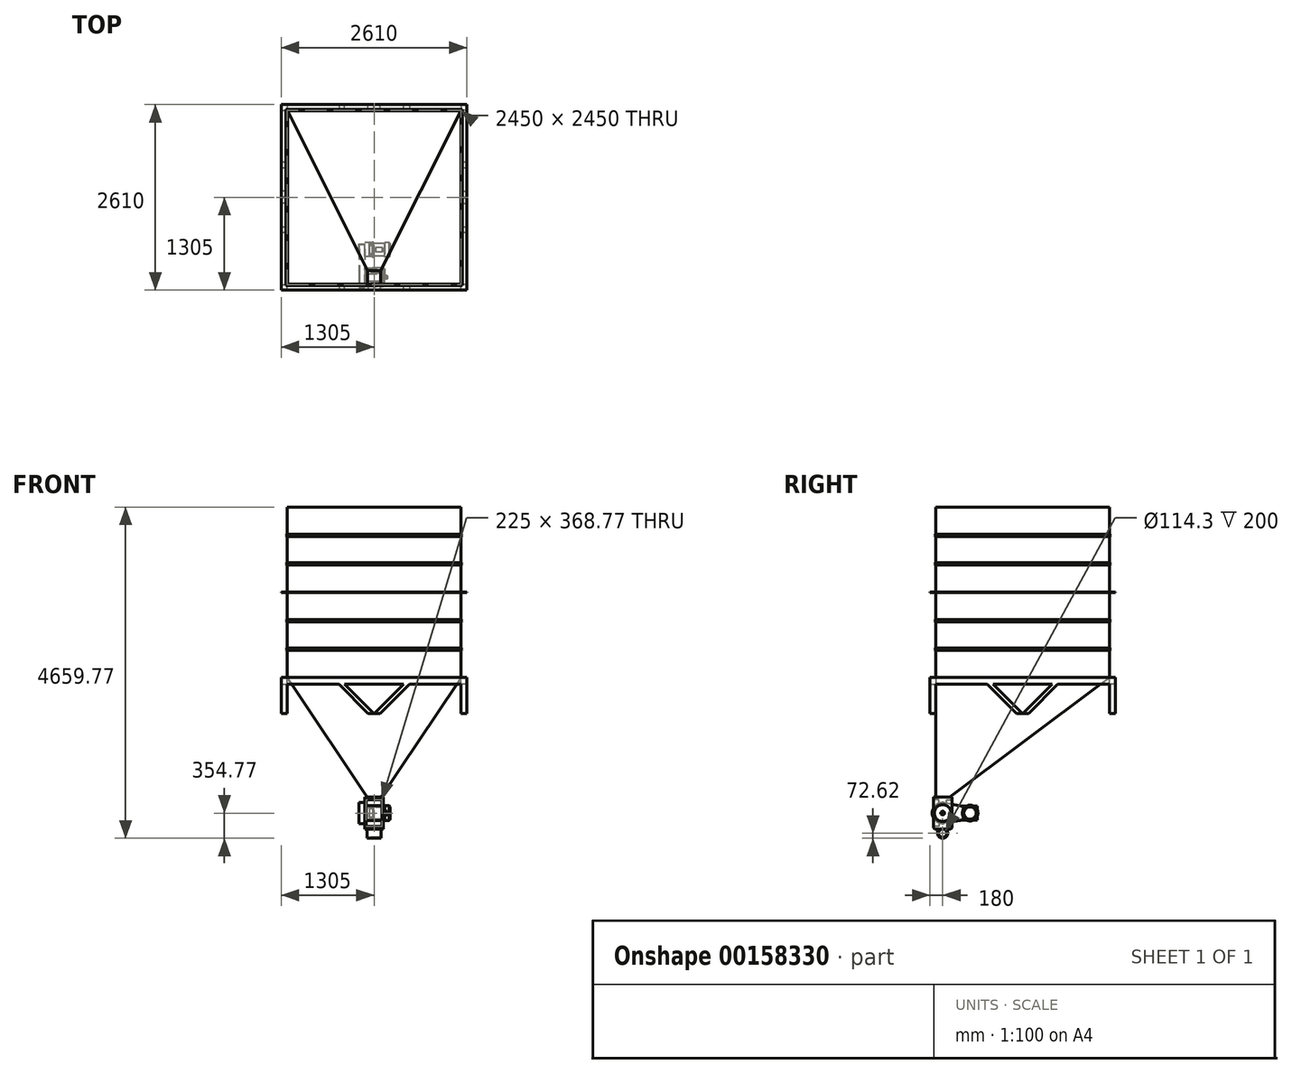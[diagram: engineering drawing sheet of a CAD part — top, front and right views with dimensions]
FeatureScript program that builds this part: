
annotation { "Feature Type Name" : "Feature", "Feature Type Description" : "" }
export const myFeature = defineFeature(function(context is Context, id is Id, definition is map)
    precondition{}
    {
        {
            var Q0;
            Q0=qCreatedBy(makeId("Top.planeOp"),FACE);
            var sketch = newSketch(context, id + "F0", { "sketchPlane" : qUnion([Q0])});
            skLineSegment(sketch, "E0.bottom", {"start": v(-1225, 1225) * mm, "end": v(1225, 1225) * mm});
            skLineSegment(sketch, "E0.top", {"start": v(-1225, -1225) * mm, "end": v(1225, -1225) * mm});
            skLineSegment(sketch, "E0.left", {"start": v(-1225, 1225) * mm, "end": v(-1225, -1225) * mm});
            skLineSegment(sketch, "E0.right", {"start": v(1225, 1225) * mm, "end": v(1225, -1225) * mm});
            skPoint(sketch, "E0.middle", {"position": v(0, 0) * mm});
            skSolve(sketch);
        }
        {
            var Q0;
            Q0=makeQuery(id+"F0.imprint","IMPRINT",FACE,{"disambiguationData":[TD([[makeQuery(id+"F0.imprint","IMPRINT",EDGE,{"derivedFrom":sQuery(id+"F0.wireOp",EDGE,"E0.bottom")}),-1.0]])]});
            extrude(context, id + "F1", {"entities" : qUnion([Q0]), "depth" : 2400 * mm});
        }
        {
            var Q0;
            Q0=makeQuery(id+"F1.opExtrude","CAP_FACE",FACE,{"disambiguationData":[OSD([sQuery(id+"F0.wireOp",EDGE,"E0.bottom"),sQuery(id+"F0.wireOp",EDGE,"E0.top"),sQuery(id+"F0.wireOp",EDGE,"E0.left"),sQuery(id+"F0.wireOp",EDGE,"E0.right")])],"isStart":true});
            cPlane(context, id + "F2", {"entities" : qUnion([Q0]), "cplaneType" : CPlaneType.OFFSET, "offset" : 1680 * mm, "width" : 150 * mm, "height" : 150 * mm});
        }
        {
            var Q0;
            Q0=qCreatedBy(id+"F2.planeOp",FACE);
            var sketch = newSketch(context, id + "F3", { "sketchPlane" : qUnion([Q0])});
            skLineSegment(sketch, "E1.bottom", {"start": v(-100, 1225) * mm, "end": v(100, 1225) * mm});
            skLineSegment(sketch, "E1.top", {"start": v(-100, 1025) * mm, "end": v(100, 1025) * mm});
            skLineSegment(sketch, "E1.left", {"start": v(100, 1225) * mm, "end": v(100, 1025) * mm});
            skLineSegment(sketch, "E1.right", {"start": v(-100, 1225) * mm, "end": v(-100, 1025) * mm});
            skPoint(sketch, "E2", {"position": v(0, 1225) * mm});
            skSolve(sketch);
        }
        {
            var Q1;
            Q1=makeQuery(id+"F1.opExtrude","CAP_FACE",FACE,{"disambiguationData":[OSD([sQuery(id+"F0.wireOp",EDGE,"E0.bottom"),sQuery(id+"F0.wireOp",EDGE,"E0.top"),sQuery(id+"F0.wireOp",EDGE,"E0.left"),sQuery(id+"F0.wireOp",EDGE,"E0.right")])],"isStart":true});
            var Q2;
            Q2=makeQuery(id+"F3.imprint","IMPRINT",FACE,{"disambiguationData":[TD([[makeQuery(id+"F3.imprint","IMPRINT",EDGE,{"derivedFrom":sQuery(id+"F3.wireOp",EDGE,"E1.bottom")}),-1.0]])]});
            loft(context, id + "F4", {"operationType" : NewBodyOperationType.ADD, "sheetProfilesArray" : [{ "sheetProfileEntities" : qUnion([Q1]) }, { "sheetProfileEntities" : qUnion([Q2]) }]});
        }
        {
            var Q0;
            Q0=makeQuery(id+"F1.opExtrude","CAP_FACE",FACE,{"disambiguationData":[OSD([sQuery(id+"F0.wireOp",EDGE,"E0.bottom"),sQuery(id+"F0.wireOp",EDGE,"E0.top"),sQuery(id+"F0.wireOp",EDGE,"E0.left"),sQuery(id+"F0.wireOp",EDGE,"E0.right")])],"isStart":false});
            extrude(context, id + "F5", {"entities" : qUnion([Q0]), "depth" : 400 * mm});
        }
        {
            var Q0;
            Q0=makeQuery(id+"F5.opExtrude","CAP_FACE",FACE,{"disambiguationData":[OSD([sQuery(id+"F0.wireOp",EDGE,"E0.bottom"),sQuery(id+"F0.wireOp",EDGE,"E0.top"),sQuery(id+"F0.wireOp",EDGE,"E0.left"),sQuery(id+"F0.wireOp",EDGE,"E0.right")])],"isStart":false});
            extrude(context, id + "F6", {"entities" : qUnion([Q0]), "depth" : 400 * mm});
        }
        {
            var Q0;
            Q0=makeQuery(id+"F1.opExtrude","CAP_FACE",FACE,{"disambiguationData":[OSD([sQuery(id+"F0.wireOp",EDGE,"E0.bottom"),sQuery(id+"F0.wireOp",EDGE,"E0.top"),sQuery(id+"F0.wireOp",EDGE,"E0.left"),sQuery(id+"F0.wireOp",EDGE,"E0.right")])],"isStart":false});
            var Q1;
            Q1=makeQuery(id+"F4.opLoft","CAP_FACE",FACE,{"disambiguationData":[OSD([makeQuery(id+"F3.imprint","IMPRINT",FACE,{"disambiguationData":[TD([[makeQuery(id+"F3.imprint","IMPRINT",EDGE,{"derivedFrom":sQuery(id+"F3.wireOp",EDGE,"E1.bottom")}),-1.0]])]})])],"isStart":true});
            shell(context, id + "F7", {"entities" : qUnion([Q0, Q1]), "thickness" : 5 * mm});
        }
        {
            var Q0;
            Q0=makeQuery(id+"F1.opExtrude","CAP_FACE",FACE,{"disambiguationData":[OSD([sQuery(id+"F0.wireOp",EDGE,"E0.bottom"),sQuery(id+"F0.wireOp",EDGE,"E0.top"),sQuery(id+"F0.wireOp",EDGE,"E0.left"),sQuery(id+"F0.wireOp",EDGE,"E0.right")])],"isStart":false});
            cPlane(context, id + "F8", {"entities" : qUnion([Q0]), "cplaneType" : CPlaneType.OFFSET, "offset" : 1200 * mm, "oppositeDirection" : true, "width" : 150 * mm, "height" : 150 * mm});
        }
        {
            var Q0;
            Q0=qCreatedBy(id+"F8.planeOp",FACE);
            var sketch = newSketch(context, id + "F9", { "sketchPlane" : qUnion([Q0])});
            skLineSegment(sketch, "E3.bottom", {"start": v(-1305, 1305) * mm, "end": v(1305, 1305) * mm});
            skLineSegment(sketch, "E3.top", {"start": v(-1305, -1305) * mm, "end": v(1305, -1305) * mm});
            skLineSegment(sketch, "E3.left", {"start": v(-1305, 1305) * mm, "end": v(-1305, -1305) * mm});
            skLineSegment(sketch, "E3.right", {"start": v(1305, 1305) * mm, "end": v(1305, -1305) * mm});
            skPoint(sketch, "E3.middle", {"position": v(0, 0) * mm});
            skLineSegment(sketch, "E4.0", {"start": v(-1225, 1225) * mm, "end": v(-1225, -1225) * mm});
            skLineSegment(sketch, "E4.1", {"start": v(-1225, 1225) * mm, "end": v(1225, 1225) * mm});
            skLineSegment(sketch, "E4.2", {"start": v(1225, 1225) * mm, "end": v(1225, -1225) * mm});
            skLineSegment(sketch, "E4.3", {"start": v(-1225, -1225) * mm, "end": v(1225, -1225) * mm});
            skSolve(sketch);
        }
        {
            var Q0;
            Q0 = qSketchRegion(id + "F9", true);
            extrude(context, id + "F10", {"entities" : qUnion([Q0]), "endBound" : BoundingType.SYMMETRIC, "depth" : 10 * mm});
        }
        {
            var Q0;
            {var subQ0=sQuery(id+"F0.wireOp",EDGE,"E0.right");var subQ1=sQuery(id+"F0.wireOp",EDGE,"E0.left");var subQ2=sQuery(id+"F0.wireOp",EDGE,"E0.bottom");Q0=makeQuery(id+"F10.boolean.opBoolean","SPLIT",FACE,{"disambiguationData":[TD([makeQuery(id+"F1.opExtrude","CAP_FACE",FACE,{"disambiguationData":[OSD([subQ2,sQuery(id+"F0.wireOp",EDGE,"E0.top"),subQ1,subQ0])],"isStart":false})])],"derivedFrom":makeQuery(id+"F1.opExtrude","SWEPT_FACE",FACE,{"disambiguationData":[OSD([subQ2])]})});}
            var sketch = newSketch(context, id + "F11", { "sketchPlane" : qUnion([Q0])});
            skLineSegment(sketch, "E5", {"start": v(-1225, 2014.14) * mm, "end": v(-1239.14, 2000) * mm});
            skLineSegment(sketch, "E6", {"start": v(-1239.14, 2000) * mm, "end": v(-1225, 1985.86) * mm});
            skLineSegment(sketch, "E7", {"start": v(-1225, 1985.86) * mm, "end": v(-1225, 2014.14) * mm});
            skPoint(sketch, "E8", {"position": v(-1225, 2000) * mm});
            skSolve(sketch);
        }
        {
            var Q0;
            Q0=makeQuery(id+"F1.opExtrude","CAP_FACE",FACE,{"disambiguationData":[OSD([sQuery(id+"F0.wireOp",EDGE,"E0.bottom"),sQuery(id+"F0.wireOp",EDGE,"E0.top"),sQuery(id+"F0.wireOp",EDGE,"E0.left"),sQuery(id+"F0.wireOp",EDGE,"E0.right")])],"isStart":false});
            var Q1;
            Q1=sQuery(id+"F11.wireOp",VERTEX,"E8");
            cPlane(context, id + "F12", {"entities" : qUnion([Q0, Q1]), "cplaneType" : CPlaneType.PLANE_POINT, "offset" : 25 * mm, "width" : 150 * mm, "height" : 150 * mm});
        }
        {
            var Q0;
            Q0=qCreatedBy(id+"F12.planeOp",FACE);
            var sketch = newSketch(context, id + "F13", { "sketchPlane" : qUnion([Q0])});
            skLineSegment(sketch, "E9.0.0", {"start": v(1225, 1225) * mm, "end": v(-1225, 1225) * mm});
            skLineSegment(sketch, "E9.0.1", {"start": v(-1225, 1225) * mm, "end": v(-1225, -1225) * mm});
            skLineSegment(sketch, "E9.0.2", {"start": v(-1225, -1225) * mm, "end": v(1225, -1225) * mm});
            skLineSegment(sketch, "E9.0.3", {"start": v(1225, -1225) * mm, "end": v(1225, 1225) * mm});
            skSolve(sketch);
        }
        {
            var Q0;
            Q0 = qSketchRegion(id + "F11", true);
            var Q1;
            Q1 = qConstructionFilter(qBodyType(qCreatedBy(id + "F13" ,EDGE), BodyType.WIRE), ConstructionObject.NO);
            sweep(context, id + "F14", {"profiles" : qUnion([Q0]), "path" : qUnion([Q1])});
        }
        {
            var Q0;
            Q0=makeQuery(id+"F1.opExtrude","CAP_FACE",FACE,{"disambiguationData":[OSD([sQuery(id+"F0.wireOp",EDGE,"E0.bottom"),sQuery(id+"F0.wireOp",EDGE,"E0.top"),sQuery(id+"F0.wireOp",EDGE,"E0.left"),sQuery(id+"F0.wireOp",EDGE,"E0.right")])],"isStart":false});
            cPlane(context, id + "F15", {"entities" : qUnion([Q0]), "cplaneType" : CPlaneType.OFFSET, "offset" : 600 * mm, "oppositeDirection" : true, "width" : 150 * mm, "height" : 150 * mm});
        }
        {
            var Q0;
            Q0=makeQuery(id+"F14.opSweep","SWEPT_BODY",BODY,{"disambiguationData":[OSD([sQuery(id+"F11.wireOp",EDGE,"E5"),sQuery(id+"F11.wireOp",EDGE,"E6"),sQuery(id+"F11.wireOp",EDGE,"E7"),sQuery(id+"F13.wireOp",EDGE,"E9.0.3")])]});
            var Q1;
            Q1=qCreatedBy(id+"F15.planeOp",FACE);
            mirror(context, id + "F16", {"entities" : qUnion([Q0]), "mirrorPlane" : qUnion([Q1])});
        }
        {
            var Q0;
            Q0=makeQuery(id+"F16.opPattern","COPY",BODY,{"derivedFrom":makeQuery(id+"F14.opSweep","SWEPT_BODY",BODY,{"disambiguationData":[OSD([sQuery(id+"F11.wireOp",EDGE,"E5"),sQuery(id+"F11.wireOp",EDGE,"E6"),sQuery(id+"F11.wireOp",EDGE,"E7"),sQuery(id+"F13.wireOp",EDGE,"E9.0.3")])]}),"instanceName":"1"});
            var Q1;
            Q1=makeQuery(id+"F14.opSweep","SWEPT_BODY",BODY,{"disambiguationData":[OSD([sQuery(id+"F11.wireOp",EDGE,"E5"),sQuery(id+"F11.wireOp",EDGE,"E6"),sQuery(id+"F11.wireOp",EDGE,"E7"),sQuery(id+"F13.wireOp",EDGE,"E9.0.3")])]});
            var Q2;
            Q2=qCreatedBy(id+"F8.planeOp",FACE);
            mirror(context, id + "F17", {"operationType" : NewBodyOperationType.ADD, "entities" : qUnion([Q0, Q1]), "mirrorPlane" : qUnion([Q2])});
        }
        {
            var Q0;
            Q0=makeQuery(id+"F1.opExtrude","CAP_FACE",FACE,{"disambiguationData":[OSD([sQuery(id+"F0.wireOp",EDGE,"E0.bottom"),sQuery(id+"F0.wireOp",EDGE,"E0.top"),sQuery(id+"F0.wireOp",EDGE,"E0.left"),sQuery(id+"F0.wireOp",EDGE,"E0.right")])],"isStart":false});
            cPlane(context, id + "F18", {"entities" : qUnion([Q0]), "cplaneType" : CPlaneType.OFFSET, "offset" : 1800 * mm, "oppositeDirection" : true, "width" : 150 * mm, "height" : 150 * mm});
        }
        {
            var Q0;
            Q0=makeQuery(id+"F10.opExtrude","SWEPT_BODY",BODY,{"disambiguationData":[OSD([sQuery(id+"F9.wireOp",EDGE,"E3.bottom"),sQuery(id+"F9.wireOp",EDGE,"E3.top"),sQuery(id+"F9.wireOp",EDGE,"E3.left"),sQuery(id+"F9.wireOp",EDGE,"E3.right")])]});
            var Q1;
            Q1=qCreatedBy(id+"F18.planeOp",FACE);
            mirror(context, id + "F19", {"entities" : qUnion([Q0]), "mirrorPlane" : qUnion([Q1])});
        }
        {
            var Q0;
            Q0=makeQuery(id+"F5.opExtrude","SWEPT_BODY",BODY,{"disambiguationData":[OSD([sQuery(id+"F0.wireOp",EDGE,"E0.bottom"),sQuery(id+"F0.wireOp",EDGE,"E0.top"),sQuery(id+"F0.wireOp",EDGE,"E0.left"),sQuery(id+"F0.wireOp",EDGE,"E0.right")])]});
            var Q1;
            Q1=makeQuery(id+"F6.opExtrude","SWEPT_BODY",BODY,{"disambiguationData":[OSD([sQuery(id+"F0.wireOp",EDGE,"E0.bottom"),sQuery(id+"F0.wireOp",EDGE,"E0.top"),sQuery(id+"F0.wireOp",EDGE,"E0.left"),sQuery(id+"F0.wireOp",EDGE,"E0.right")])]});
            deleteBodies(context, id + "F20", {"entities" : qUnion([Q0, Q1])});
        }
        {
            var Q0;
            Q0=makeQuery(id+"F1.opExtrude","CAP_FACE",FACE,{"disambiguationData":[OSD([sQuery(id+"F0.wireOp",EDGE,"E0.bottom"),sQuery(id+"F0.wireOp",EDGE,"E0.top"),sQuery(id+"F0.wireOp",EDGE,"E0.left"),sQuery(id+"F0.wireOp",EDGE,"E0.right")])],"isStart":false});
            var sketch = newSketch(context, id + "F21", { "sketchPlane" : qUnion([Q0])});
            skLineSegment(sketch, "E10.bottom", {"start": v(-1536.15, 1536.15) * mm, "end": v(1536.15, 1536.15) * mm});
            skLineSegment(sketch, "E10.top", {"start": v(-1536.15, -1536.15) * mm, "end": v(1536.15, -1536.15) * mm});
            skLineSegment(sketch, "E10.left", {"start": v(-1536.15, 1536.15) * mm, "end": v(-1536.15, -1536.15) * mm});
            skLineSegment(sketch, "E10.right", {"start": v(1536.15, 1536.15) * mm, "end": v(1536.15, -1536.15) * mm});
            skPoint(sketch, "E10.middle", {"position": v(0, 0) * mm});
            skSolve(sketch);
        }
        {
            var Q0;
            Q0=makeQuery(id+"F4.opLoft","CAP_FACE",FACE,{"disambiguationData":[OSD([makeQuery(id+"F3.imprint","IMPRINT",FACE,{"disambiguationData":[TD([[makeQuery(id+"F3.imprint","IMPRINT",EDGE,{"derivedFrom":sQuery(id+"F3.wireOp",EDGE,"E1.bottom")}),-1.0]])]})])],"isStart":true});
            var sketch = newSketch(context, id + "F22", { "sketchPlane" : qUnion([Q0])});
            skLineSegment(sketch, "E11.0", {"start": v(-130, 1255) * mm, "end": v(-130, 995) * mm});
            skLineSegment(sketch, "E11.1", {"start": v(130, 1255) * mm, "end": v(-130, 1255) * mm});
            skLineSegment(sketch, "E11.2", {"start": v(130, 995) * mm, "end": v(130, 1255) * mm});
            skLineSegment(sketch, "E11.3", {"start": v(-130, 995) * mm, "end": v(130, 995) * mm});
            skSolve(sketch);
        }
        {
            var Q0;
            Q0 = qSketchRegion(id + "F22", true);
            extrude(context, id + "F23", {"entities" : qUnion([Q0]), "depth" : 450 * mm});
        }
        {
            var Q0;
            Q0=makeQuery(id+"F23.opExtrude","SWEPT_FACE",FACE,{"disambiguationData":[OSD([sQuery(id+"F22.wireOp",EDGE,"E11.2")])]});
            var sketch = newSketch(context, id + "F24", { "sketchPlane" : qUnion([Q0])});
            skCircle(sketch, "E12", {"center": v(-1125, -1905) * mm, "radius": 118.36 * mm});
            skPoint(sketch, "E13", {"position": v(-1255, -1905) * mm});
            skPoint(sketch, "E14", {"position": v(-1125, -1680) * mm});
            skSolve(sketch);
        }
        {
            var Q0;
            Q0 = qSketchRegion(id + "F24", true);
            extrude(context, id + "F25", {"entities" : qUnion([Q0]), "operationType" : NewBodyOperationType.ADD, "depth" : 17.5 * mm});
        }
        {
            var Q0;
            Q0=makeQuery(id+"F25.opExtrude","CAP_FACE",FACE,{"disambiguationData":[OSD([sQuery(id+"F24.wireOp",EDGE,"E12")])],"isStart":false});
            var sketch = newSketch(context, id + "F26", { "sketchPlane" : qUnion([Q0])});
            skCircle(sketch, "E15", {"center": v(-1125, -1905) * mm, "radius": 25.57 * mm});
            skSolve(sketch);
        }
        {
            var Q0;
            Q0 = qSketchRegion(id + "F26", true);
            extrude(context, id + "F27", {"entities" : qUnion([Q0]), "operationType" : NewBodyOperationType.ADD, "depth" : 40 * mm});
        }
        {
            var Q0;
            Q0=makeQuery(id+"F27.opExtrude","CAP_EDGE",EDGE,{"disambiguationData":[OSD([sQuery(id+"F26.wireOp",EDGE,"E15")])],"isStart":false});
            chamfer(context, id + "F28", {"entities" : qUnion([Q0]), "width" : 5 * mm, "tangentPropagation" : true});
        }
        {
            var Q0;
            Q0=qCreatedBy(makeId("Right.planeOp"),FACE);
            var sketch = newSketch(context, id + "F29", { "sketchPlane" : qUnion([Q0])});
            skArc(sketch, "E16", {"start": v(-1177.5, -1798.91) * mm, "mid": v(-1243.36, -1905) * mm, "end": v(-1177.5, -2011.09) * mm});
            skLineSegment(sketch, "E17", {"start": v(-1125, -1680) * mm, "end": v(-1125, -2130) * mm, "construction": true});
            skArc(sketch, "E18.MirrorCS", {"start": v(-1072.5, -1798.91) * mm, "mid": v(-1006.64, -1905) * mm, "end": v(-1072.5, -2011.09) * mm});
            skLineSegment(sketch, "E19", {"start": v(-1177.5, -1798.91) * mm, "end": v(-1177.5, -1720.61) * mm});
            skLineSegment(sketch, "E20", {"start": v(-1255, -1905) * mm, "end": v(-995, -1905) * mm, "construction": true});
            skLineSegment(sketch, "E21", {"start": v(-1177.5, -1720.61) * mm, "end": v(-1255, -1720.61) * mm});
            skLineSegment(sketch, "E22", {"start": v(-1255, -1720.61) * mm, "end": v(-1255, -1905) * mm});
            skLineSegment(sketch, "E23.MirrorCS", {"start": v(-1072.5, -1798.91) * mm, "end": v(-1072.5, -1720.61) * mm});
            skLineSegment(sketch, "E24.MirrorCS", {"start": v(-1072.5, -1720.61) * mm, "end": v(-995, -1720.61) * mm});
            skLineSegment(sketch, "E25.MirrorCS", {"start": v(-995, -1720.61) * mm, "end": v(-995, -1905) * mm});
            skLineSegment(sketch, "E26.MirrorCS", {"start": v(-995, -2089.39) * mm, "end": v(-995, -1905) * mm});
            skLineSegment(sketch, "E27.MirrorCS", {"start": v(-1072.5, -2089.39) * mm, "end": v(-995, -2089.39) * mm});
            skLineSegment(sketch, "E28.MirrorCS", {"start": v(-1072.5, -2011.09) * mm, "end": v(-1072.5, -2089.39) * mm});
            skLineSegment(sketch, "E29.MirrorCS", {"start": v(-1177.5, -2011.09) * mm, "end": v(-1177.5, -2089.39) * mm});
            skLineSegment(sketch, "E30.MirrorCS", {"start": v(-1177.5, -2089.39) * mm, "end": v(-1255, -2089.39) * mm});
            skLineSegment(sketch, "E31.MirrorCS", {"start": v(-1255, -2089.39) * mm, "end": v(-1255, -1905) * mm});
            skSolve(sketch);
        }
        {
            var Q0;
            Q0 = qSketchRegion(id + "F29", true);
            extrude(context, id + "F30", {"entities" : qUnion([Q0]), "operationType" : NewBodyOperationType.REMOVE, "endBound" : BoundingType.SYMMETRIC, "oppositeDirection" : true, "depth" : 225 * mm});
        }
        {
            var Q0;
            Q0=makeQuery(id+"F23.opExtrude","SWEPT_FACE",FACE,{"disambiguationData":[OSD([sQuery(id+"F22.wireOp",EDGE,"E11.0")])]});
            var sketch = newSketch(context, id + "F31", { "sketchPlane" : qUnion([Q0])});
            skLineSegment(sketch, "E32", {"start": v(724.05, -1826.48) * mm, "end": v(1099.3, -1759.97) * mm});
            skLineSegment(sketch, "E33", {"start": v(724.05, -1983.52) * mm, "end": v(1099.3, -2050.03) * mm});
            skArc(sketch, "E34", {"start": v(724.05, -1826.48) * mm, "mid": v(658.22, -1905) * mm, "end": v(724.05, -1983.52) * mm});
            skArc(sketch, "E35", {"start": v(724.05, -1983.52) * mm, "mid": v(817.7, -1905) * mm, "end": v(724.05, -1826.48) * mm, "construction": true});
            skArc(sketch, "E36", {"start": v(1099.3, -1759.97) * mm, "mid": v(977.7, -1905) * mm, "end": v(1099.3, -2050.03) * mm, "construction": true});
            skArc(sketch, "E37", {"start": v(1099.3, -2050.03) * mm, "mid": v(1272.3, -1905) * mm, "end": v(1099.3, -1759.97) * mm});
            skSolve(sketch);
        }
        {
            var Q0;
            Q0 = qSketchRegion(id + "F31", true);
            extrude(context, id + "F32", {"entities" : qUnion([Q0]), "depth" : 85 * mm});
        }
        {
            var Q0;
            Q0=makeQuery(id+"F32.opExtrude","CAP_FACE",FACE,{"disambiguationData":[OSD([sQuery(id+"F31.wireOp",EDGE,"E32"),sQuery(id+"F31.wireOp",EDGE,"E33"),sQuery(id+"F31.wireOp",EDGE,"E34"),sQuery(id+"F31.wireOp",EDGE,"E37")])],"isStart":true});
            shell(context, id + "F33", {"entities" : qUnion([Q0]), "thickness" : 5 * mm});
        }
        {
            var Q0;
            Q0=makeQuery(id+"F32.opExtrude","CAP_FACE",FACE,{"disambiguationData":[OSD([sQuery(id+"F31.wireOp",EDGE,"E32"),sQuery(id+"F31.wireOp",EDGE,"E33"),sQuery(id+"F31.wireOp",EDGE,"E34"),sQuery(id+"F31.wireOp",EDGE,"E37")])],"isStart":true});
            var sketch = newSketch(context, id + "F34", { "sketchPlane" : qUnion([Q0])});
            skLineSegment(sketch, "E38.bottom", {"start": v(-836.4, -1806.57) * mm, "end": v(-639.53, -1806.57) * mm});
            skLineSegment(sketch, "E38.top", {"start": v(-836.4, -2003.43) * mm, "end": v(-639.53, -2003.43) * mm});
            skLineSegment(sketch, "E38.left", {"start": v(-836.4, -1806.57) * mm, "end": v(-836.4, -2003.43) * mm});
            skLineSegment(sketch, "E38.right", {"start": v(-639.53, -1806.57) * mm, "end": v(-639.53, -2003.43) * mm});
            skPoint(sketch, "E38.middle", {"position": v(-737.97, -1905) * mm});
            skSolve(sketch);
        }
        {
            var Q0;
            Q0 = qSketchRegion(id + "F34", true);
            extrude(context, id + "F35", {"entities" : qUnion([Q0]), "depth" : 60 * mm});
        }
        {
            var Q0;
            Q0=makeQuery(id+"F35.opExtrude","CAP_FACE",FACE,{"disambiguationData":[OSD([sQuery(id+"F34.wireOp",EDGE,"E38.bottom"),sQuery(id+"F34.wireOp",EDGE,"E38.top"),sQuery(id+"F34.wireOp",EDGE,"E38.left"),sQuery(id+"F34.wireOp",EDGE,"E38.right")])],"isStart":false});
            var sketch = newSketch(context, id + "F36", { "sketchPlane" : qUnion([Q0])});
            skArc(sketch, "E39", {"start": v(-817, -1846.33) * mm, "mid": v(-836.4, -1905) * mm, "end": v(-817, -1963.67) * mm});
            skLineSegment(sketch, "E40", {"start": v(-679.3, -1825.97) * mm, "end": v(-658.76, -1813.38) * mm});
            skLineSegment(sketch, "E41", {"start": v(-737.97, -1905) * mm, "end": v(-639.53, -1806.57) * mm, "construction": true});
            skLineSegment(sketch, "E42", {"start": v(-658.76, -1813.38) * mm, "end": v(-652.56, -1819.59) * mm});
            skLineSegment(sketch, "E43.MirrorCS", {"start": v(-646.35, -1825.8) * mm, "end": v(-652.56, -1819.59) * mm});
            skLineSegment(sketch, "E44.MirrorCS", {"start": v(-658.93, -1846.33) * mm, "end": v(-646.35, -1825.8) * mm});
            skLineSegment(sketch, "E45", {"start": v(-737.97, -1806.57) * mm, "end": v(-737.97, -2003.43) * mm, "construction": true});
            skLineSegment(sketch, "E46", {"start": v(-639.53, -1905) * mm, "end": v(-836.4, -1905) * mm, "construction": true});
            skLineSegment(sketch, "E47.MirrorCS", {"start": v(-796.64, -1825.97) * mm, "end": v(-817.17, -1813.38) * mm});
            skLineSegment(sketch, "E48.MirrorCS", {"start": v(-817, -1846.33) * mm, "end": v(-829.58, -1825.8) * mm});
            skLineSegment(sketch, "E49.MirrorCS", {"start": v(-829.58, -1825.8) * mm, "end": v(-823.38, -1819.59) * mm});
            skLineSegment(sketch, "E50.MirrorCS", {"start": v(-817.17, -1813.38) * mm, "end": v(-823.38, -1819.59) * mm});
            skLineSegment(sketch, "E51.MirrorCS", {"start": v(-658.93, -1963.67) * mm, "end": v(-646.35, -1984.2) * mm});
            skLineSegment(sketch, "E52.MirrorCS", {"start": v(-658.76, -1996.62) * mm, "end": v(-652.56, -1990.41) * mm});
            skLineSegment(sketch, "E53.MirrorCS", {"start": v(-679.3, -1984.03) * mm, "end": v(-658.76, -1996.62) * mm});
            skLineSegment(sketch, "E54.MirrorCS", {"start": v(-796.64, -1984.03) * mm, "end": v(-817.17, -1996.62) * mm});
            skLineSegment(sketch, "E55.MirrorCS", {"start": v(-817.17, -1996.62) * mm, "end": v(-823.38, -1990.41) * mm});
            skLineSegment(sketch, "E56.MirrorCS", {"start": v(-829.58, -1984.2) * mm, "end": v(-823.38, -1990.41) * mm});
            skLineSegment(sketch, "E57.MirrorCS", {"start": v(-817, -1963.67) * mm, "end": v(-829.58, -1984.2) * mm});
            skLineSegment(sketch, "E58.MirrorCS", {"start": v(-646.35, -1984.2) * mm, "end": v(-652.56, -1990.41) * mm});
            skArc(sketch, "E59.trimOffspring", {"start": v(-679.3, -1825.97) * mm, "mid": v(-737.97, -1806.57) * mm, "end": v(-796.64, -1825.97) * mm});
            skArc(sketch, "E60.trimOffspring", {"start": v(-658.93, -1963.67) * mm, "mid": v(-639.53, -1905) * mm, "end": v(-658.93, -1846.33) * mm});
            skArc(sketch, "E61.trimOffspring", {"start": v(-796.64, -1984.03) * mm, "mid": v(-737.97, -2003.43) * mm, "end": v(-679.3, -1984.03) * mm});
            skSolve(sketch);
        }
        {
            var Q0;
            Q0 = qSketchRegion(id + "F36", true);
            extrude(context, id + "F37", {"entities" : qUnion([Q0]), "operationType" : NewBodyOperationType.ADD, "depth" : 50 * mm});
        }
        {
            var Q0;
            Q0=makeQuery(id+"F37.opExtrude","CAP_FACE",FACE,{"disambiguationData":[OSD([sQuery(id+"F36.wireOp",EDGE,"E39"),sQuery(id+"F36.wireOp",EDGE,"E40"),sQuery(id+"F36.wireOp",EDGE,"E42"),sQuery(id+"F36.wireOp",EDGE,"E43.MirrorCS"),sQuery(id+"F36.wireOp",EDGE,"E44.MirrorCS"),sQuery(id+"F36.wireOp",EDGE,"E47.MirrorCS"),sQuery(id+"F36.wireOp",EDGE,"E48.MirrorCS"),sQuery(id+"F36.wireOp",EDGE,"E49.MirrorCS"),sQuery(id+"F36.wireOp",EDGE,"E50.MirrorCS"),sQuery(id+"F36.wireOp",EDGE,"E51.MirrorCS"),sQuery(id+"F36.wireOp",EDGE,"E52.MirrorCS"),sQuery(id+"F36.wireOp",EDGE,"E53.MirrorCS"),sQuery(id+"F36.wireOp",EDGE,"E54.MirrorCS"),sQuery(id+"F36.wireOp",EDGE,"E55.MirrorCS"),sQuery(id+"F36.wireOp",EDGE,"E56.MirrorCS"),sQuery(id+"F36.wireOp",EDGE,"E57.MirrorCS"),sQuery(id+"F36.wireOp",EDGE,"E58.MirrorCS"),sQuery(id+"F36.wireOp",EDGE,"E59.trimOffspring"),sQuery(id+"F36.wireOp",EDGE,"E60.trimOffspring"),sQuery(id+"F36.wireOp",EDGE,"E61.trimOffspring")])],"isStart":false});
            var sketch = newSketch(context, id + "F38", { "sketchPlane" : qUnion([Q0])});
            skCircle(sketch, "E62", {"center": v(-737.97, -1905) * mm, "radius": 110.24 * mm});
            skSolve(sketch);
        }
        {
            var Q0;
            Q0 = qSketchRegion(id + "F38", true);
            extrude(context, id + "F39", {"entities" : qUnion([Q0]), "operationType" : NewBodyOperationType.ADD, "depth" : 7.5 * mm});
        }
        {
            var Q0;
            Q0=makeQuery(id+"F39.opExtrude","CAP_FACE",FACE,{"disambiguationData":[OSD([sQuery(id+"F38.wireOp",EDGE,"E62")])],"isStart":false});
            var sketch = newSketch(context, id + "F40", { "sketchPlane" : qUnion([Q0])});
            skCircle(sketch, "E63", {"center": v(-737.97, -1905) * mm, "radius": 86.74 * mm});
            skSolve(sketch);
        }
        {
            var Q0;
            Q0 = qSketchRegion(id + "F40", true);
            extrude(context, id + "F41", {"entities" : qUnion([Q0]), "operationType" : NewBodyOperationType.ADD, "depth" : 160 * mm});
        }
        {
            var Q0;
            Q0=makeQuery(id+"F41.opExtrude","CAP_FACE",FACE,{"disambiguationData":[OSD([sQuery(id+"F40.wireOp",EDGE,"E63")])],"isStart":false});
            var sketch = newSketch(context, id + "F42", { "sketchPlane" : qUnion([Q0])});
            skCircle(sketch, "E64", {"center": v(-737.97, -1905) * mm, "radius": 103.35 * mm});
            skSolve(sketch);
        }
        {
            var Q0;
            Q0 = qSketchRegion(id + "F42", true);
            extrude(context, id + "F43", {"entities" : qUnion([Q0]), "operationType" : NewBodyOperationType.ADD, "depth" : 77.5 * mm});
        }
        {
            var Q0;
            Q0=makeQuery(id+"F43.opExtrude","CAP_EDGE",EDGE,{"disambiguationData":[OSD([sQuery(id+"F42.wireOp",EDGE,"E64")])],"isStart":false});
            chamfer(context, id + "F44", {"entities" : qUnion([Q0]), "width" : 15 * mm, "tangentPropagation" : true});
        }
        {
            var Q0;
            Q0=makeQuery(id+"F35.opExtrude","SWEPT_FACE",FACE,{"disambiguationData":[OSD([sQuery(id+"F34.wireOp",EDGE,"E38.bottom")])]});
            var sketch = newSketch(context, id + "F45", { "sketchPlane" : qUnion([Q0])});
            skLineSegment(sketch, "E65.bottom", {"start": v(115.81, -707.31) * mm, "end": v(22.17, -707.31) * mm});
            skLineSegment(sketch, "E65.top", {"start": v(115.81, -768.62) * mm, "end": v(22.17, -768.62) * mm});
            skLineSegment(sketch, "E65.left", {"start": v(115.81, -707.31) * mm, "end": v(115.81, -768.62) * mm});
            skLineSegment(sketch, "E65.right", {"start": v(22.17, -707.31) * mm, "end": v(22.17, -768.62) * mm});
            skPoint(sketch, "E65.middle", {"position": v(68.99, -737.97) * mm});
            skPoint(sketch, "E66", {"position": v(-130, -737.97) * mm});
            skSolve(sketch);
        }
        {
            var Q0;
            Q0 = qSketchRegion(id + "F45", true);
            extrude(context, id + "F46", {"entities" : qUnion([Q0]), "operationType" : NewBodyOperationType.ADD, "endBound" : BoundingType.UP_TO_NEXT, "oppositeDirection" : true, "depth" : 25 * mm});
        }
        {
            var Q0;
            Q0=qCreatedBy(makeId("Right.planeOp"),FACE);
            var sketch = newSketch(context, id + "F47", { "sketchPlane" : qUnion([Q0])});
            skCircle(sketch, "E67", {"center": v(-1125, -2187.15) * mm, "radius": 57.15 * mm});
            skCircle(sketch, "E68.0", {"center": v(-1125, -1905) * mm, "radius": 118.36 * mm, "construction": true});
            skArc(sketch, "E69", {"start": v(-1195.78, -2170.89) * mm, "mid": v(-1125, -2259.77) * mm, "end": v(-1054.22, -2170.89) * mm});
            skArc(sketch, "E70", {"start": v(-1021.67, -2130) * mm, "mid": v(-1047.8, -2142.6) * mm, "end": v(-1054.22, -2170.89) * mm});
            skArc(sketch, "E71", {"start": v(-1195.78, -2170.89) * mm, "mid": v(-1202.2, -2142.6) * mm, "end": v(-1228.33, -2130) * mm});
            skLineSegment(sketch, "E72", {"start": v(-1228.33, -2163.4) * mm, "end": v(-1021.67, -2163.4) * mm, "construction": true});
            skLineSegment(sketch, "E73", {"start": v(-1228.33, -2130) * mm, "end": v(-1228.33, -2117.94) * mm});
            skLineSegment(sketch, "E74", {"start": v(-1228.33, -2117.94) * mm, "end": v(-1021.67, -2117.94) * mm});
            skLineSegment(sketch, "E75", {"start": v(-1021.67, -2117.94) * mm, "end": v(-1021.67, -2130) * mm});
            skSolve(sketch);
        }
        {
            var Q0;
            {var subQ3=sQuery(id+"F47.wireOp",EDGE,"E67");Q0=makeQuery(id+"F47.imprint","IMPRINT",FACE,{"disambiguationData":[TD([[makeQuery(id+"F47.imprint","IMPRINT",EDGE,{"derivedFrom":subQ3}),-1.0]])]});}
            extrude(context, id + "F48", {"entities" : qUnion([Q0]), "operationType" : NewBodyOperationType.ADD, "endBound" : BoundingType.SYMMETRIC, "depth" : 200 * mm});
        }
        {
            var Q0;
            Q0=makeQuery(id+"F23.opExtrude","CAP_EDGE",EDGE,{"disambiguationData":[OSD([sQuery(id+"F22.wireOp",EDGE,"E11.3")])],"isStart":false});
            var Q1;
            Q1=makeQuery(id+"F23.opExtrude","CAP_EDGE",EDGE,{"disambiguationData":[OSD([sQuery(id+"F22.wireOp",EDGE,"E11.1")])],"isStart":false});
            chamfer(context, id + "F49", {"entities" : qUnion([Q0, Q1]), "width" : 20 * mm, "tangentPropagation" : true});
        }
        {
            var Q0;
            Q0=makeQuery(id+"F19.opPattern","COPY",FACE,{"derivedFrom":makeQuery(id+"F10.opExtrude","CAP_FACE",FACE,{"disambiguationData":[OSD([sQuery(id+"F9.wireOp",EDGE,"E3.bottom"),sQuery(id+"F9.wireOp",EDGE,"E3.top"),sQuery(id+"F9.wireOp",EDGE,"E3.left"),sQuery(id+"F9.wireOp",EDGE,"E3.right"),sQuery(id+"F9.wireOp",EDGE,"E4.0"),sQuery(id+"F9.wireOp",EDGE,"E4.1"),sQuery(id+"F9.wireOp",EDGE,"E4.2"),sQuery(id+"F9.wireOp",EDGE,"E4.3")])],"isStart":false}),"instanceName":"1"});
            var sketch = newSketch(context, id + "F50", { "sketchPlane" : qUnion([Q0])});
            skLineSegment(sketch, "E76.bottom", {"start": v(-1305, 1305) * mm, "end": v(-1225, 1305) * mm});
            skLineSegment(sketch, "E76.top", {"start": v(-1305, 1225) * mm, "end": v(-1225, 1225) * mm});
            skLineSegment(sketch, "E76.left", {"start": v(-1305, 1305) * mm, "end": v(-1305, 1225) * mm});
            skLineSegment(sketch, "E76.right", {"start": v(-1225, 1305) * mm, "end": v(-1225, 1225) * mm});
            skLineSegment(sketch, "E77.bottom", {"start": v(1305, 1305) * mm, "end": v(1225, 1305) * mm});
            skLineSegment(sketch, "E77.top", {"start": v(1305, 1225) * mm, "end": v(1225, 1225) * mm});
            skLineSegment(sketch, "E77.left", {"start": v(1305, 1305) * mm, "end": v(1305, 1225) * mm});
            skLineSegment(sketch, "E77.right", {"start": v(1225, 1305) * mm, "end": v(1225, 1225) * mm});
            skLineSegment(sketch, "E78.bottom", {"start": v(1305, -1305) * mm, "end": v(1225, -1305) * mm});
            skLineSegment(sketch, "E78.top", {"start": v(1305, -1225) * mm, "end": v(1225, -1225) * mm});
            skLineSegment(sketch, "E78.left", {"start": v(1305, -1305) * mm, "end": v(1305, -1225) * mm});
            skLineSegment(sketch, "E78.right", {"start": v(1225, -1305) * mm, "end": v(1225, -1225) * mm});
            skLineSegment(sketch, "E79.bottom", {"start": v(-1305, -1305) * mm, "end": v(-1225, -1305) * mm});
            skLineSegment(sketch, "E79.top", {"start": v(-1305, -1225) * mm, "end": v(-1225, -1225) * mm});
            skLineSegment(sketch, "E79.left", {"start": v(-1305, -1305) * mm, "end": v(-1305, -1225) * mm});
            skLineSegment(sketch, "E79.right", {"start": v(-1225, -1305) * mm, "end": v(-1225, -1225) * mm});
            skSolve(sketch);
        }
        {
            var Q0;
            Q0 = qSketchRegion(id + "F50", true);
            extrude(context, id + "F51", {"entities" : qUnion([Q0]), "operationType" : NewBodyOperationType.ADD, "depth" : 500 * mm});
        }
        {
            var Q0;
            Q0=makeQuery(id+"F51.boolean.opBoolean","MERGE",FACE,{"derivedFrom":[makeQuery(id+"F19.opPattern","COPY",FACE,{"derivedFrom":makeQuery(id+"F10.opExtrude","SWEPT_FACE",FACE,{"disambiguationData":[OSD([sQuery(id+"F9.wireOp",EDGE,"E3.top")])]}),"instanceName":"1"}),makeQuery(id+"F51.opExtrude","SWEPT_FACE",FACE,{"disambiguationData":[OSD([sQuery(id+"F50.wireOp",EDGE,"E76.bottom")])]}),makeQuery(id+"F51.opExtrude","SWEPT_FACE",FACE,{"disambiguationData":[OSD([sQuery(id+"F50.wireOp",EDGE,"E77.bottom")])]})]});
            var sketch = newSketch(context, id + "F52", { "sketchPlane" : qUnion([Q0])});
            skLineSegment(sketch, "E80", {"start": v(-585, -5) * mm, "end": v(-85, -505) * mm});
            skLineSegment(sketch, "E81", {"start": v(-85, -505) * mm, "end": v(-5, -505) * mm});
            skLineSegment(sketch, "E82", {"start": v(-5, -505) * mm, "end": v(-505, -5) * mm});
            skLineSegment(sketch, "E83", {"start": v(-505, -5) * mm, "end": v(-585, -5) * mm});
            skLineSegment(sketch, "E84.MirrorCS", {"start": v(5, -505) * mm, "end": v(505, -5) * mm});
            skLineSegment(sketch, "E85.MirrorCS", {"start": v(85, -505) * mm, "end": v(5, -505) * mm});
            skLineSegment(sketch, "E86.MirrorCS", {"start": v(585, -5) * mm, "end": v(85, -505) * mm});
            skLineSegment(sketch, "E87.MirrorCS", {"start": v(505, -5) * mm, "end": v(585, -5) * mm});
            skSolve(sketch);
        }
        {
            var Q0;
            Q0 = qSketchRegion(id + "F52", true);
            var Q1;
            Q1=makeQuery(id+"F51.opExtrude","SWEPT_FACE",FACE,{"disambiguationData":[OSD([sQuery(id+"F50.wireOp",EDGE,"E76.top")])]});
            extrude(context, id + "F53", {"entities" : qUnion([Q0]), "endBound" : BoundingType.UP_TO_SURFACE, "oppositeDirection" : true, "endBoundEntityFace" : qUnion([Q1]), "depth" : 25 * mm});
        }
        {
            var Q0;
            Q0=makeQuery(id+"F53.opExtrude","SWEPT_BODY",BODY,{"disambiguationData":[OSD([sQuery(id+"F52.wireOp",EDGE,"E80"),sQuery(id+"F52.wireOp",EDGE,"E81"),sQuery(id+"F52.wireOp",EDGE,"E82"),sQuery(id+"F52.wireOp",EDGE,"E83")])]});
            var Q1;
            Q1=makeQuery(id+"F53.opExtrude","SWEPT_BODY",BODY,{"disambiguationData":[OSD([sQuery(id+"F52.wireOp",EDGE,"E84.MirrorCS"),sQuery(id+"F52.wireOp",EDGE,"E85.MirrorCS"),sQuery(id+"F52.wireOp",EDGE,"E86.MirrorCS"),sQuery(id+"F52.wireOp",EDGE,"E87.MirrorCS")])]});
            var Q2;
            Q2=qCreatedBy(makeId("Front.planeOp"),FACE);
            mirror(context, id + "F54", {"operationType" : NewBodyOperationType.ADD, "entities" : qUnion([Q0, Q1]), "mirrorPlane" : qUnion([Q2])});
        }
        {
            var Q0;
            Q0=makeQuery(id+"F51.boolean.opBoolean","MERGE",FACE,{"derivedFrom":[makeQuery(id+"F19.opPattern","COPY",FACE,{"derivedFrom":makeQuery(id+"F10.opExtrude","SWEPT_FACE",FACE,{"disambiguationData":[OSD([sQuery(id+"F9.wireOp",EDGE,"E3.left")])]}),"instanceName":"1"}),makeQuery(id+"F51.opExtrude","SWEPT_FACE",FACE,{"disambiguationData":[OSD([sQuery(id+"F50.wireOp",EDGE,"E76.left")])]}),makeQuery(id+"F51.opExtrude","SWEPT_FACE",FACE,{"disambiguationData":[OSD([sQuery(id+"F50.wireOp",EDGE,"E79.left")])]})]});
            var sketch = newSketch(context, id + "F55", { "sketchPlane" : qUnion([Q0])});
            skLineSegment(sketch, "E88", {"start": v(-585, -5) * mm, "end": v(-85, -505) * mm});
            skLineSegment(sketch, "E89", {"start": v(-85, -505) * mm, "end": v(-5, -505) * mm});
            skLineSegment(sketch, "E90", {"start": v(-5, -505) * mm, "end": v(-505, -5) * mm});
            skLineSegment(sketch, "E91", {"start": v(-505, -5) * mm, "end": v(-585, -5) * mm});
            skLineSegment(sketch, "E92.MirrorCS", {"start": v(85, -505) * mm, "end": v(5, -505) * mm});
            skLineSegment(sketch, "E93.MirrorCS", {"start": v(5, -505) * mm, "end": v(505, -5) * mm});
            skLineSegment(sketch, "E94.MirrorCS", {"start": v(585, -5) * mm, "end": v(85, -505) * mm});
            skLineSegment(sketch, "E95.MirrorCS", {"start": v(505, -5) * mm, "end": v(585, -5) * mm});
            skSolve(sketch);
        }
        {
            var Q0;
            Q0 = qSketchRegion(id + "F55", true);
            var Q1;
            Q1=makeQuery(id+"F51.opExtrude","SWEPT_FACE",FACE,{"disambiguationData":[OSD([sQuery(id+"F50.wireOp",EDGE,"E79.right")])]});
            extrude(context, id + "F56", {"entities" : qUnion([Q0]), "endBound" : BoundingType.UP_TO_SURFACE, "oppositeDirection" : true, "endBoundEntityFace" : qUnion([Q1]), "depth" : 25 * mm});
        }
        {
            var Q0;
            Q0=makeQuery(id+"F56.opExtrude","SWEPT_BODY",BODY,{"disambiguationData":[OSD([sQuery(id+"F55.wireOp",EDGE,"E88"),sQuery(id+"F55.wireOp",EDGE,"E89"),sQuery(id+"F55.wireOp",EDGE,"E90"),sQuery(id+"F55.wireOp",EDGE,"E91")])]});
            var Q1;
            Q1=makeQuery(id+"F56.opExtrude","SWEPT_BODY",BODY,{"disambiguationData":[OSD([sQuery(id+"F55.wireOp",EDGE,"E92.MirrorCS"),sQuery(id+"F55.wireOp",EDGE,"E93.MirrorCS"),sQuery(id+"F55.wireOp",EDGE,"E94.MirrorCS"),sQuery(id+"F55.wireOp",EDGE,"E95.MirrorCS")])]});
            var Q2;
            Q2=qCreatedBy(makeId("Right.planeOp"),FACE);
            mirror(context, id + "F57", {"operationType" : NewBodyOperationType.ADD, "entities" : qUnion([Q0, Q1]), "mirrorPlane" : qUnion([Q2])});
        }
        {
            var Q0;
            Q0=makeQuery(id+"F19.opPattern","COPY",FACE,{"derivedFrom":makeQuery(id+"F10.opExtrude","CAP_FACE",FACE,{"disambiguationData":[OSD([sQuery(id+"F9.wireOp",EDGE,"E3.bottom"),sQuery(id+"F9.wireOp",EDGE,"E3.top"),sQuery(id+"F9.wireOp",EDGE,"E3.left"),sQuery(id+"F9.wireOp",EDGE,"E3.right"),sQuery(id+"F9.wireOp",EDGE,"E4.0"),sQuery(id+"F9.wireOp",EDGE,"E4.1"),sQuery(id+"F9.wireOp",EDGE,"E4.2"),sQuery(id+"F9.wireOp",EDGE,"E4.3")])],"isStart":true}),"instanceName":"1"});
            extrude(context, id + "F58", {"entities" : qUnion([Q0]), "operationType" : NewBodyOperationType.ADD, "oppositeDirection" : true, "depth" : 100 * mm});
        }
    });
